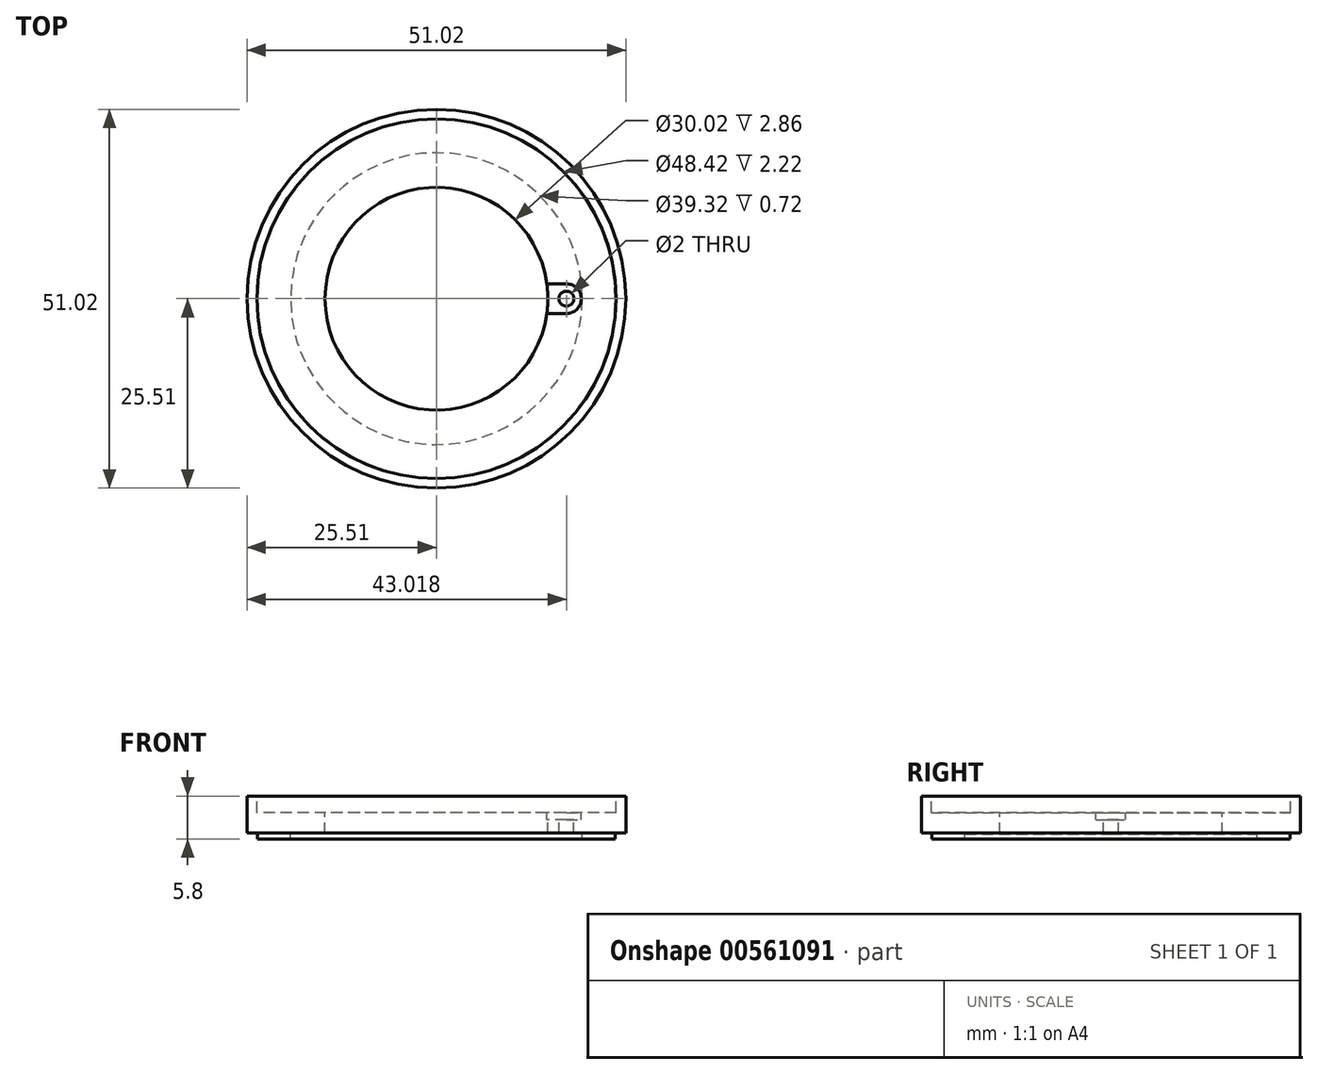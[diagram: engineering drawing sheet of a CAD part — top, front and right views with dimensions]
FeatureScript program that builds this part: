
annotation { "Feature Type Name" : "Feature", "Feature Type Description" : "" }
export const myFeature = defineFeature(function(context is Context, id is Id, definition is map)
    precondition{}
    {
        {
            var Q0;
            Q0=qCreatedBy(makeId("Front.planeOp"),FACE);
            var sketch = newSketch(context, id + "F0", { "sketchPlane" : qUnion([Q0])});
            skLineSegment(sketch, "E0.bottom", {"start": v(-25.5, 5.8) * mm, "end": v(-24.2, 5.8) * mm});
            skLineSegment(sketch, "E0.top", {"start": v(-24.1, 0) * mm, "end": v(-19.66, 0) * mm});
            skLineSegment(sketch, "E0.left", {"start": v(-25.5, 5.8) * mm, "end": v(-25.5, 0.85) * mm});
            skLineSegment(sketch, "E0.right", {"start": v(-15, 3.58) * mm, "end": v(-15, 0.72) * mm});
            skLineSegment(sketch, "E1.top", {"start": v(-15, 3.58) * mm, "end": v(-24.2, 3.58) * mm});
            skLineSegment(sketch, "E1.right", {"start": v(-24.2, 5.8) * mm, "end": v(-24.2, 3.58) * mm});
            skLineSegment(sketch, "E2.top", {"start": v(-15, 0.72) * mm, "end": v(-19.66, 0.72) * mm});
            skLineSegment(sketch, "E2.right", {"start": v(-19.66, 0) * mm, "end": v(-19.66, 0.72) * mm});
            skLineSegment(sketch, "E3.top", {"start": v(-25.5, 0.85) * mm, "end": v(-24.1, 0.85) * mm});
            skLineSegment(sketch, "E3.right", {"start": v(-24.1, 0) * mm, "end": v(-24.1, 0.85) * mm});
            skSolve(sketch);
        }
        {
            var Q0;
            Q0=qCreatedBy(makeId("Front.planeOp"),FACE);
            var sketch = newSketch(context, id + "F1", { "sketchPlane" : qUnion([Q0])});
            skLineSegment(sketch, "E4", {"start": v(0, 10) * mm, "end": v(0, 0) * mm});
            skSolve(sketch);
        }
        {
            var Q0;
            Q0=makeQuery(id+"F0.imprint","IMPRINT",FACE,{"disambiguationData":[TD([[makeQuery(id+"F0.imprint","IMPRINT",EDGE,{"derivedFrom":sQuery(id+"F0.wireOp",EDGE,"E0.bottom")}),-1.0]])]});
            var Q1;
            Q1=sQuery(id+"F1.wireOp",EDGE,"E4");
            revolve(context, id + "F2", {"entities" : qUnion([Q0]), "axis" : qUnion([Q1]), "revolveType" : RevolveType.FULL});
        }
        {
            var Q0;
            Q0=makeQuery(id+"F2.opRevolve","SWEPT_FACE",FACE,{"disambiguationData":[OSD([sQuery(id+"F0.wireOp",EDGE,"E1.top")])]});
            var sketch = newSketch(context, id + "F3", { "sketchPlane" : qUnion([Q0])});
            skArc(sketch, "E5", {"start": v(17.5, -2) * mm, "mid": v(19.5, 0) * mm, "end": v(17.5, 2) * mm});
            skPoint(sketch, "E6", {"position": v(15, 0) * mm});
            skLineSegment(sketch, "E7", {"start": v(17.5, 2) * mm, "end": v(14.87, 2) * mm});
            skLineSegment(sketch, "E8", {"start": v(17.5, -2) * mm, "end": v(14.87, -2) * mm});
            skPoint(sketch, "E9", {"position": v(0, 0) * mm});
            skCircle(sketch, "E10", {"center": v(17.5, 0) * mm, "radius": 1 * mm});
            skSolve(sketch);
        }
        {
            var Q0;
            Q0=makeQuery(id+"F3.imprint","IMPRINT",FACE,{"disambiguationData":[TD([[makeQuery(id+"F3.imprint","IMPRINT",EDGE,{"derivedFrom":sQuery(id+"F3.wireOp",EDGE,"E5")}),1.0]])]});
            extrude(context, id + "F4", {"entities" : qUnion([Q0]), "operationType" : NewBodyOperationType.REMOVE, "oppositeDirection" : true, "depth" : 1 * mm, "offsetDistance" : 25 * mm});
        }
        {
            var Q0;
            Q0=makeQuery(id+"F3.imprint","IMPRINT",FACE,{"disambiguationData":[TD([[makeQuery(id+"F3.imprint","IMPRINT",EDGE,{"derivedFrom":sQuery(id+"F3.wireOp",EDGE,"E10")}),1.0]])]});
            extrude(context, id + "F5", {"entities" : qUnion([Q0]), "operationType" : NewBodyOperationType.REMOVE, "oppositeDirection" : true, "depth" : 2.86 * mm, "offsetDistance" : 25 * mm});
        }
    });
